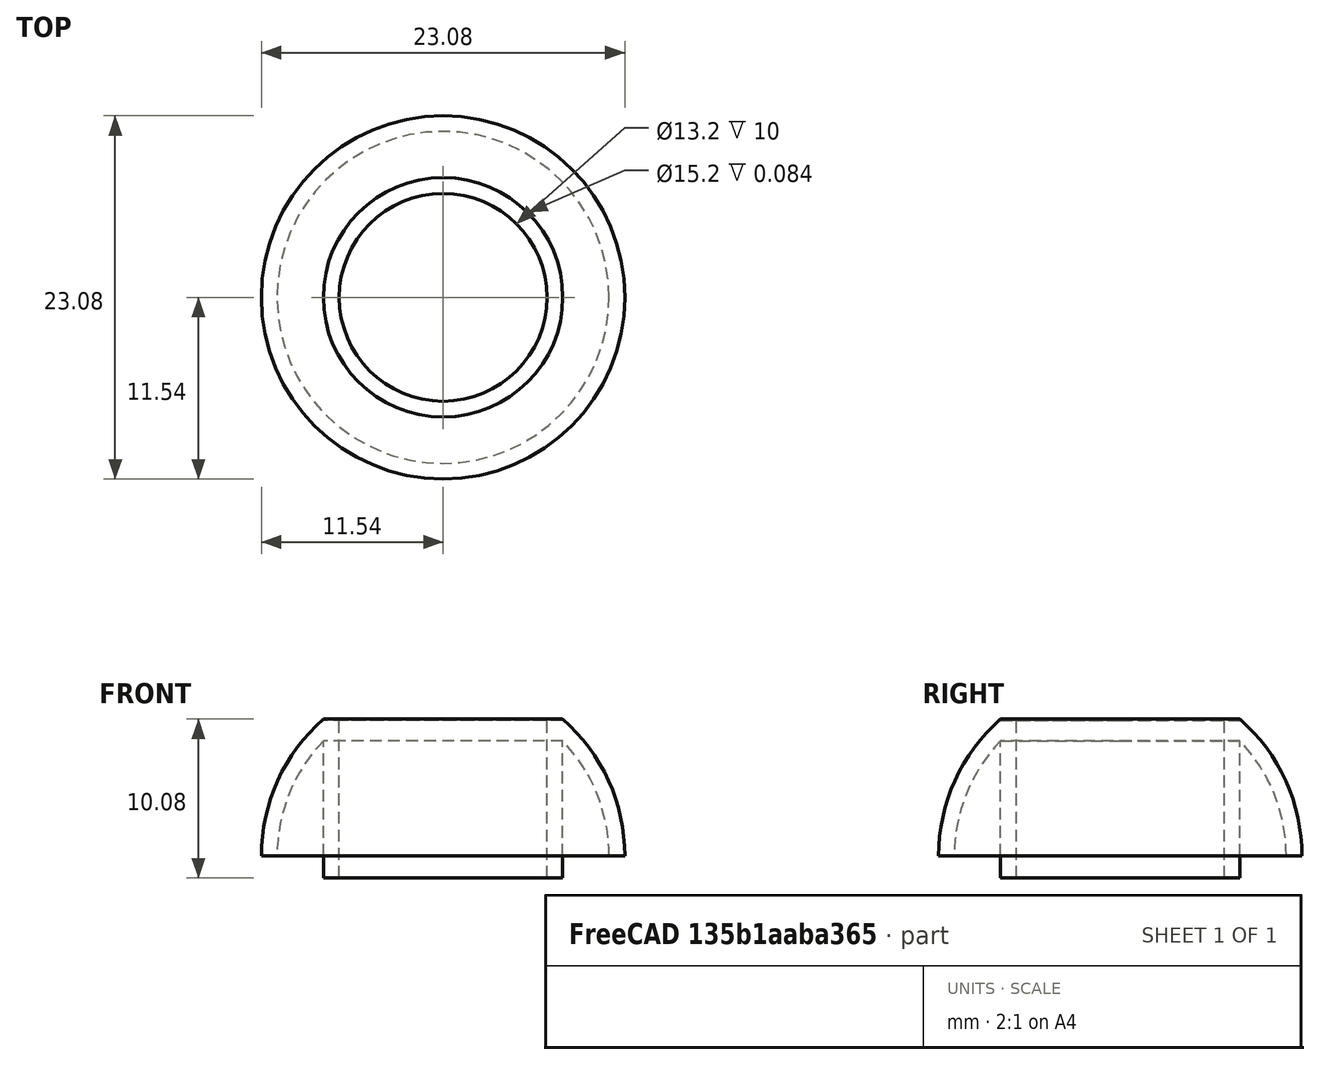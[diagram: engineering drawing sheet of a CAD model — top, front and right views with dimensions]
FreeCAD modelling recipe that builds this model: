
FCSTD DOCUMENT  (FreeCAD 0.18R16131 (Git))
Label: seguro
License: All rights reserved
LicenseURL: http://en.wikipedia.org/wiki/All_rights_reserved
objects: Part::Cylinder×3, Part::Cut×3, Part::Sphere×2, Part::MultiFuse×1
note: 9 computed .brp shape members not serialized (recipe doc carries the construction recipe); baked Part::Feature solids carry a one-line shape summary decoded from their .brp

FEATURE [Part::Sphere] Sphere  label="Esfera"
  Angle1 = 0
  Angle2 = 90
  Angle3 = 360
  AttacherType = Attacher::AttachEngine3D
  Radius = 11.54
FEATURE [Part::Sphere] Sphere001  label="Esfera001"
  Angle1 = -90
  Angle2 = 90
  Angle3 = 360
  AttacherType = Attacher::AttachEngine3D
  Radius = 10.54
FEATURE [Part::Cylinder] Cylinder  label="CilindroParaCorte"
  Angle = 360
  AttacherType = Attacher::AttachEngine3D
  Height = 10
  Placement = pos=(0,0,2) rot=(0,0,1;0rad)
  Radius = 7.6
FEATURE [Part::Cylinder] Cylinder001  label="CilindroGuia1"
  Angle = 360
  AttacherType = Attacher::AttachEngine3D
  Height = 10
  Placement = pos=(0,0,2) rot=(0,0,1;0rad)
  Radius = 7.6
FEATURE [Part::Cylinder] Cylinder002  label="CilindroGuia002"
  Angle = 360
  AttacherType = Attacher::AttachEngine3D
  Height = 10
  Placement = pos=(0,0,2) rot=(0,0,1;0rad)
  Radius = 6.6
FEATURE [Part::Cut] Cut
  Base = -> Cylinder001
  Placement = pos=(0,0,-3.4) rot=(0,0,1;0rad)
  Tool = -> Cylinder002
FEATURE [Part::Cut] Cut001
  Base = -> Sphere
  Tool = -> Cylinder
FEATURE [Part::Cut] Cut002
  Base = -> Cut001
  Tool = -> Sphere001
FEATURE [Part::MultiFuse] Fusion
  Shapes = -> [Cut,Cut002]
